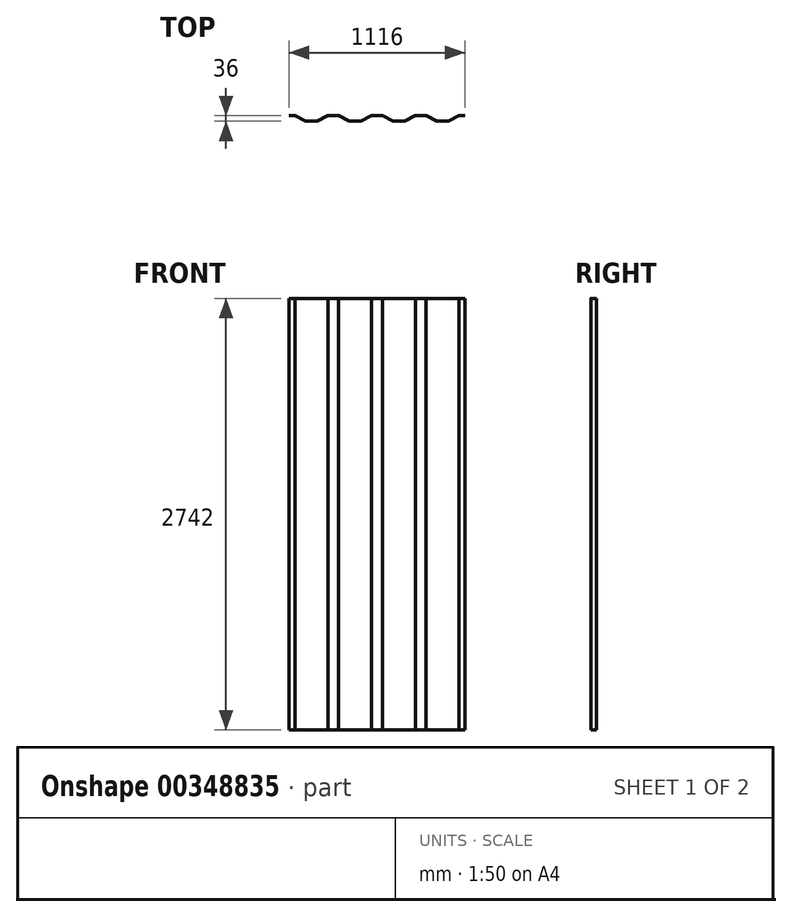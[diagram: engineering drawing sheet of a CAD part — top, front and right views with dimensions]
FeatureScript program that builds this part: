
annotation { "Feature Type Name" : "Feature", "Feature Type Description" : "" }
export const myFeature = defineFeature(function(context is Context, id is Id, definition is map)
    precondition{}
    {
        {
            var Q0;
            Q0=qCreatedBy(makeId("Top.planeOp"),FACE);
            var sketch = newSketch(context, id + "F0", { "sketchPlane" : qUnion([Q0])});
            skLineSegment(sketch, "E0", {"start": v(0, 0) * mm, "end": v(1116, 0) * mm});
            skLineSegment(sketch, "E1", {"start": v(0, 15.22) * mm, "end": v(37, 15.22) * mm});
            skLineSegment(sketch, "E2", {"start": v(37, 15.22) * mm, "end": v(105, 15.22) * mm});
            skLineSegment(sketch, "E3", {"start": v(105, 15.22) * mm, "end": v(177, 15.22) * mm});
            skLineSegment(sketch, "E4", {"start": v(177, 15.22) * mm, "end": v(245, 15.22) * mm});
            skLineSegment(sketch, "E5", {"start": v(245, 15.22) * mm, "end": v(315, 15.22) * mm});
            skLineSegment(sketch, "E6", {"start": v(315, 15.22) * mm, "end": v(383, 15.22) * mm});
            skLineSegment(sketch, "E7", {"start": v(383, 15.22) * mm, "end": v(455, 15.22) * mm});
            skLineSegment(sketch, "E8", {"start": v(455, 15.22) * mm, "end": v(523, 15.22) * mm});
            skLineSegment(sketch, "E9", {"start": v(523, 15.22) * mm, "end": v(593, 15.22) * mm});
            skLineSegment(sketch, "E10", {"start": v(593, 15.22) * mm, "end": v(661, 15.22) * mm});
            skLineSegment(sketch, "E11", {"start": v(661, 15.22) * mm, "end": v(733, 15.22) * mm});
            skLineSegment(sketch, "E12", {"start": v(733, 15.22) * mm, "end": v(801, 15.22) * mm});
            skLineSegment(sketch, "E13", {"start": v(801, 15.22) * mm, "end": v(871, 15.22) * mm});
            skLineSegment(sketch, "E14", {"start": v(871, 15.22) * mm, "end": v(939, 15.22) * mm});
            skLineSegment(sketch, "E15", {"start": v(939, 15.22) * mm, "end": v(1011, 15.22) * mm});
            skLineSegment(sketch, "E16", {"start": v(1011, 15.22) * mm, "end": v(1079, 15.22) * mm});
            skLineSegment(sketch, "E17", {"start": v(1079, 15.22) * mm, "end": v(1116, 15.22) * mm});
            skLineSegment(sketch, "E18", {"start": v(1116, 15.22) * mm, "end": v(1116, 51.22) * mm});
            skLineSegment(sketch, "E19", {"start": v(1124.7, 15.22) * mm, "end": v(1124.7, 16.82) * mm});
            skLineSegment(sketch, "E20", {"start": v(1116, 51.22) * mm, "end": v(1080.2, 51.22) * mm});
            skLineSegment(sketch, "E21", {"start": v(1077.94, 50.68) * mm, "end": v(1012.06, 17.36) * mm});
            skLineSegment(sketch, "E22", {"start": v(1009.8, 16.82) * mm, "end": v(940.2, 16.82) * mm});
            skLineSegment(sketch, "E23", {"start": v(937.94, 17.36) * mm, "end": v(872.06, 50.68) * mm});
            skLineSegment(sketch, "E24", {"start": v(869.8, 51.22) * mm, "end": v(802.2, 51.22) * mm});
            skLineSegment(sketch, "E25", {"start": v(799.94, 50.68) * mm, "end": v(734.06, 17.36) * mm});
            skLineSegment(sketch, "E26", {"start": v(731.8, 16.82) * mm, "end": v(662.2, 16.82) * mm});
            skLineSegment(sketch, "E27", {"start": v(659.94, 17.36) * mm, "end": v(594.06, 50.68) * mm});
            skLineSegment(sketch, "E28", {"start": v(591.8, 51.22) * mm, "end": v(524.2, 51.22) * mm});
            skLineSegment(sketch, "E29", {"start": v(456.06, 17.36) * mm, "end": v(521.94, 50.68) * mm});
            skLineSegment(sketch, "E30", {"start": v(453.8, 16.82) * mm, "end": v(384.2, 16.82) * mm});
            skLineSegment(sketch, "E31", {"start": v(381.94, 17.36) * mm, "end": v(316.06, 50.68) * mm});
            skLineSegment(sketch, "E32", {"start": v(313.8, 51.22) * mm, "end": v(246.2, 51.22) * mm});
            skLineSegment(sketch, "E33", {"start": v(243.94, 50.68) * mm, "end": v(178.06, 17.36) * mm});
            skLineSegment(sketch, "E34", {"start": v(175.8, 16.82) * mm, "end": v(106.2, 16.82) * mm});
            skLineSegment(sketch, "E35", {"start": v(103.94, 17.36) * mm, "end": v(38.06, 50.68) * mm});
            skLineSegment(sketch, "E36", {"start": v(35.8, 51.22) * mm, "end": v(0, 51.22) * mm});
            skPoint(sketch, "E37.visualSharp", {"position": v(1079, 51.22) * mm});
            skArc(sketch, "E37.filletArc", {"start": v(1080.2, 51.22) * mm, "mid": v(1079.03, 51.09) * mm, "end": v(1077.94, 50.68) * mm});
            skPoint(sketch, "E38.visualSharp", {"position": v(1011, 16.82) * mm});
            skArc(sketch, "E38.filletArc", {"start": v(1009.8, 16.82) * mm, "mid": v(1010.97, 16.96) * mm, "end": v(1012.06, 17.36) * mm});
            skPoint(sketch, "E39.visualSharp", {"position": v(939, 16.82) * mm});
            skArc(sketch, "E39.filletArc", {"start": v(937.94, 17.36) * mm, "mid": v(939.03, 16.96) * mm, "end": v(940.2, 16.82) * mm});
            skPoint(sketch, "E40.visualSharp", {"position": v(871, 51.22) * mm});
            skArc(sketch, "E40.filletArc", {"start": v(872.06, 50.68) * mm, "mid": v(870.97, 51.09) * mm, "end": v(869.8, 51.22) * mm});
            skPoint(sketch, "E41.visualSharp", {"position": v(801, 51.22) * mm});
            skArc(sketch, "E41.filletArc", {"start": v(802.2, 51.22) * mm, "mid": v(801.03, 51.09) * mm, "end": v(799.94, 50.68) * mm});
            skPoint(sketch, "E42.visualSharp", {"position": v(733, 16.82) * mm});
            skArc(sketch, "E42.filletArc", {"start": v(731.8, 16.82) * mm, "mid": v(732.97, 16.96) * mm, "end": v(734.06, 17.36) * mm});
            skPoint(sketch, "E43.visualSharp", {"position": v(661, 16.82) * mm});
            skArc(sketch, "E43.filletArc", {"start": v(659.94, 17.36) * mm, "mid": v(661.03, 16.96) * mm, "end": v(662.2, 16.82) * mm});
            skPoint(sketch, "E44.visualSharp", {"position": v(593, 51.22) * mm});
            skArc(sketch, "E44.filletArc", {"start": v(594.06, 50.68) * mm, "mid": v(592.97, 51.09) * mm, "end": v(591.8, 51.22) * mm});
            skPoint(sketch, "E45.visualSharp", {"position": v(523, 51.22) * mm});
            skArc(sketch, "E45.filletArc", {"start": v(524.2, 51.22) * mm, "mid": v(523.03, 51.09) * mm, "end": v(521.94, 50.68) * mm});
            skPoint(sketch, "E46.visualSharp", {"position": v(455, 16.82) * mm});
            skArc(sketch, "E46.filletArc", {"start": v(453.8, 16.82) * mm, "mid": v(454.97, 16.96) * mm, "end": v(456.06, 17.36) * mm});
            skPoint(sketch, "E47.visualSharp", {"position": v(383, 16.82) * mm});
            skArc(sketch, "E47.filletArc", {"start": v(381.94, 17.36) * mm, "mid": v(383.03, 16.96) * mm, "end": v(384.2, 16.82) * mm});
            skPoint(sketch, "E48.visualSharp", {"position": v(315, 51.22) * mm});
            skArc(sketch, "E48.filletArc", {"start": v(316.06, 50.68) * mm, "mid": v(314.97, 51.09) * mm, "end": v(313.8, 51.22) * mm});
            skPoint(sketch, "E49.visualSharp", {"position": v(245, 51.22) * mm});
            skArc(sketch, "E49.filletArc", {"start": v(246.2, 51.22) * mm, "mid": v(245.03, 51.09) * mm, "end": v(243.94, 50.68) * mm});
            skPoint(sketch, "E50.visualSharp", {"position": v(177, 16.82) * mm});
            skArc(sketch, "E50.filletArc", {"start": v(175.8, 16.82) * mm, "mid": v(176.97, 16.96) * mm, "end": v(178.06, 17.36) * mm});
            skPoint(sketch, "E51.visualSharp", {"position": v(37, 51.22) * mm});
            skArc(sketch, "E51.filletArc", {"start": v(38.06, 50.68) * mm, "mid": v(36.97, 51.09) * mm, "end": v(35.8, 51.22) * mm});
            skPoint(sketch, "E52.visualSharp", {"position": v(105, 16.82) * mm});
            skArc(sketch, "E52.filletArc", {"start": v(103.94, 17.36) * mm, "mid": v(105.03, 16.96) * mm, "end": v(106.2, 16.82) * mm});
            skLineSegment(sketch, "E53.0", {"start": v(36.62, 49.62) * mm, "end": v(0, 49.62) * mm});
            skLineSegment(sketch, "E53.1", {"start": v(103.21, 15.93) * mm, "end": v(36.62, 49.62) * mm});
            skArc(sketch, "E53.2", {"start": v(103.21, 15.93) * mm, "mid": v(104.66, 15.4) * mm, "end": v(106.2, 15.22) * mm});
            skLineSegment(sketch, "E53.3", {"start": v(731.8, 15.22) * mm, "end": v(662.2, 15.22) * mm});
            skArc(sketch, "E53.4", {"start": v(731.8, 15.22) * mm, "mid": v(733.34, 15.4) * mm, "end": v(734.79, 15.93) * mm});
            skLineSegment(sketch, "E53.5", {"start": v(801.38, 49.62) * mm, "end": v(734.79, 15.93) * mm});
            skLineSegment(sketch, "E53.6", {"start": v(870.62, 49.62) * mm, "end": v(801.38, 49.62) * mm});
            skLineSegment(sketch, "E53.7", {"start": v(937.21, 15.93) * mm, "end": v(870.62, 49.62) * mm});
            skArc(sketch, "E53.8", {"start": v(937.21, 15.93) * mm, "mid": v(938.66, 15.4) * mm, "end": v(940.2, 15.22) * mm});
            skLineSegment(sketch, "E53.9", {"start": v(1116, 49.62) * mm, "end": v(1079.38, 49.62) * mm});
            skLineSegment(sketch, "E53.10", {"start": v(1079.38, 49.62) * mm, "end": v(1012.79, 15.93) * mm});
            skArc(sketch, "E53.11", {"start": v(1009.8, 15.22) * mm, "mid": v(1011.34, 15.4) * mm, "end": v(1012.79, 15.93) * mm});
            skLineSegment(sketch, "E53.12", {"start": v(1009.8, 15.22) * mm, "end": v(940.2, 15.22) * mm});
            skArc(sketch, "E53.13", {"start": v(659.21, 15.93) * mm, "mid": v(660.66, 15.4) * mm, "end": v(662.2, 15.22) * mm});
            skLineSegment(sketch, "E53.14", {"start": v(659.21, 15.93) * mm, "end": v(592.62, 49.62) * mm});
            skLineSegment(sketch, "E53.15", {"start": v(592.62, 49.62) * mm, "end": v(523.38, 49.62) * mm});
            skLineSegment(sketch, "E53.16", {"start": v(456.79, 15.93) * mm, "end": v(523.38, 49.62) * mm});
            skArc(sketch, "E53.17", {"start": v(453.8, 15.22) * mm, "mid": v(455.34, 15.4) * mm, "end": v(456.79, 15.93) * mm});
            skLineSegment(sketch, "E53.18", {"start": v(453.8, 15.22) * mm, "end": v(384.2, 15.22) * mm});
            skArc(sketch, "E53.19", {"start": v(381.21, 15.93) * mm, "mid": v(382.66, 15.4) * mm, "end": v(384.2, 15.22) * mm});
            skLineSegment(sketch, "E53.20", {"start": v(381.21, 15.93) * mm, "end": v(314.62, 49.62) * mm});
            skLineSegment(sketch, "E53.21", {"start": v(314.62, 49.62) * mm, "end": v(245.38, 49.62) * mm});
            skLineSegment(sketch, "E53.22", {"start": v(245.38, 49.62) * mm, "end": v(178.79, 15.93) * mm});
            skArc(sketch, "E53.23", {"start": v(175.8, 15.22) * mm, "mid": v(177.34, 15.4) * mm, "end": v(178.79, 15.93) * mm});
            skLineSegment(sketch, "E53.24", {"start": v(175.8, 15.22) * mm, "end": v(106.2, 15.22) * mm});
            skLineSegment(sketch, "E54", {"start": v(0, 51.22) * mm, "end": v(0, 49.62) * mm});
            skSolve(sketch);
        }
        {
            var Q0;
            {var subQ1=sQuery(id+"F0.wireOp",EDGE,"E20");Q0=makeQuery(id+"F0.imprint","IMPRINT",FACE,{"disambiguationData":[TD([[makeQuery(id+"F0.imprint","IMPRINT",EDGE,{"derivedFrom":subQ1}),1.0]])]});}
            extrude(context, id + "F1", {"entities" : qUnion([Q0]), "depth" : 2742 * mm});
        }
    });
